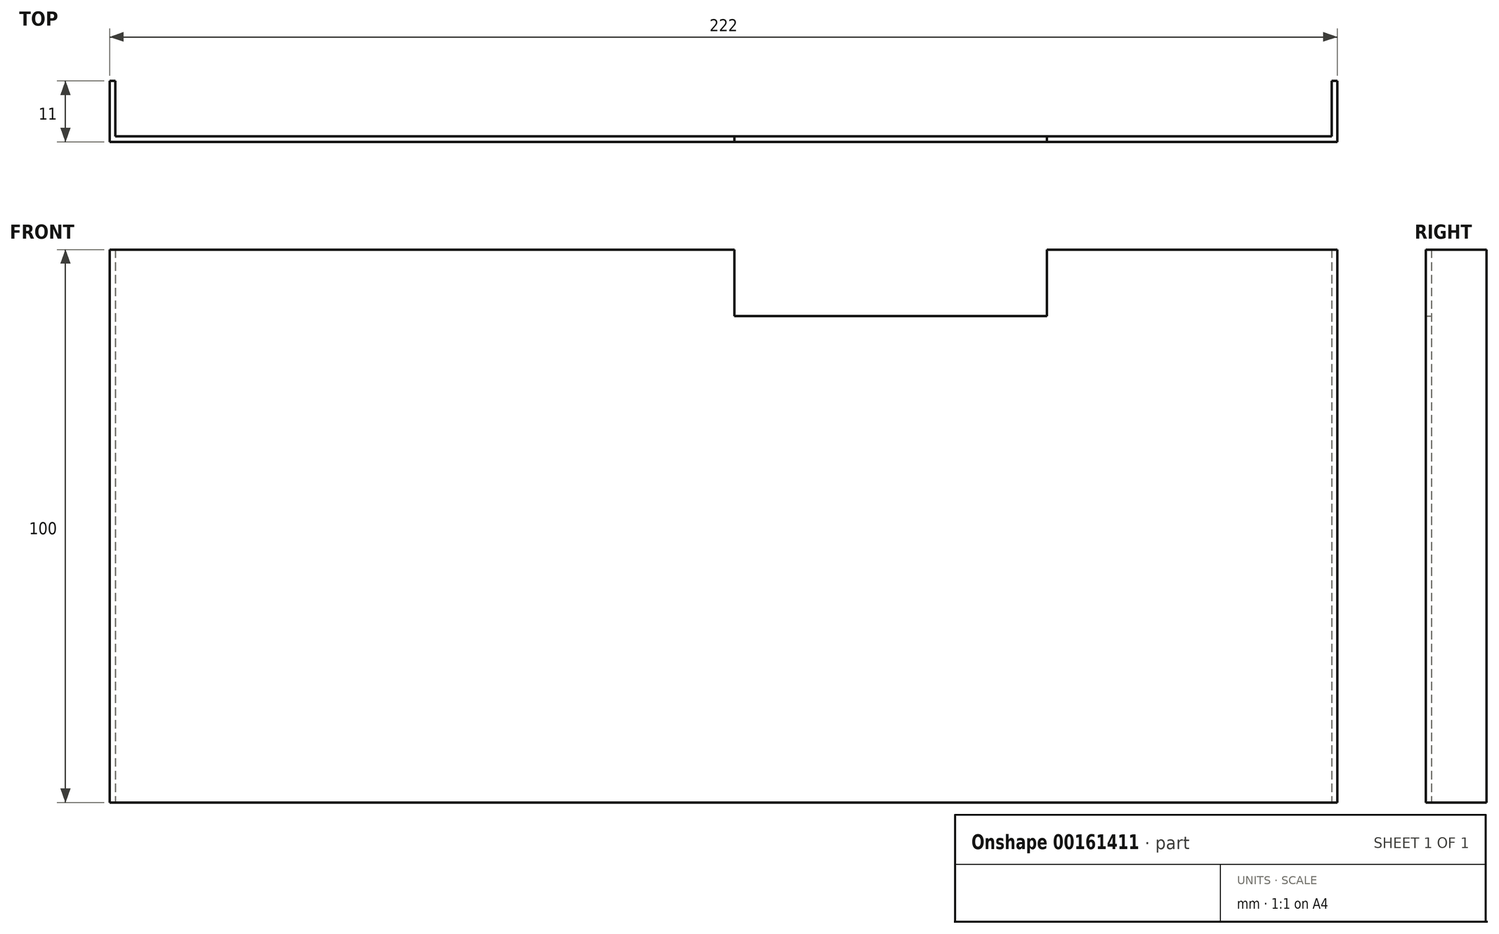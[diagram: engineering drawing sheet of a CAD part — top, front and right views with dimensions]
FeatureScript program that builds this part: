
annotation { "Feature Type Name" : "Feature", "Feature Type Description" : "" }
export const myFeature = defineFeature(function(context is Context, id is Id, definition is map)
    precondition{}
    {
        {
            var Q0;
            Q0=qCreatedBy(makeId("Front.planeOp"),FACE);
            var sketch = newSketch(context, id + "F0", { "sketchPlane" : qUnion([Q0])});
            skLineSegment(sketch, "E0.bottom", {"start": v(111, 45.92) * mm, "end": v(58.5, 45.92) * mm});
            skLineSegment(sketch, "E0.top", {"start": v(111, -54.08) * mm, "end": v(-111, -54.08) * mm});
            skLineSegment(sketch, "E0.left", {"start": v(111, 45.92) * mm, "end": v(111, -54.08) * mm});
            skLineSegment(sketch, "E0.right", {"start": v(-111, 45.92) * mm, "end": v(-111, -54.08) * mm});
            skPoint(sketch, "E0.middle", {"position": v(0, -4.08) * mm});
            skLineSegment(sketch, "E1.top", {"start": v(58.5, 33.92) * mm, "end": v(2, 33.92) * mm});
            skLineSegment(sketch, "E1.left", {"start": v(58.5, 45.92) * mm, "end": v(58.5, 33.92) * mm});
            skLineSegment(sketch, "E1.right", {"start": v(2, 45.92) * mm, "end": v(2, 33.92) * mm});
            skLineSegment(sketch, "E2.trimOffspring", {"start": v(2, 45.92) * mm, "end": v(-111, 45.92) * mm});
            skSolve(sketch);
        }
        {
            var Q0;
            Q0 = qSketchRegion(id + "F0", true);
            extrude(context, id + "F1", {"entities" : qUnion([Q0]), "depth" : 1 * mm});
        }
        {
            var Q0;
            Q0=makeQuery(id+"F1.opExtrude","CAP_FACE",FACE,{"disambiguationData":[OSD([sQuery(id+"F0.wireOp",EDGE,"E0.bottom"),sQuery(id+"F0.wireOp",EDGE,"E0.top"),sQuery(id+"F0.wireOp",EDGE,"E0.left"),sQuery(id+"F0.wireOp",EDGE,"E0.right"),sQuery(id+"F0.wireOp",EDGE,"E1.top"),sQuery(id+"F0.wireOp",EDGE,"E1.left"),sQuery(id+"F0.wireOp",EDGE,"E1.right"),sQuery(id+"F0.wireOp",EDGE,"E2.trimOffspring")])],"isStart":true});
            var sketch = newSketch(context, id + "F2", { "sketchPlane" : qUnion([Q0])});
            skLineSegment(sketch, "E3.bottom", {"start": v(-111, 45.92) * mm, "end": v(-110, 45.92) * mm});
            skLineSegment(sketch, "E3.top", {"start": v(-111, -54.08) * mm, "end": v(-110, -54.08) * mm});
            skLineSegment(sketch, "E3.left", {"start": v(-111, 45.92) * mm, "end": v(-111, -54.08) * mm});
            skLineSegment(sketch, "E3.right", {"start": v(-110, 45.92) * mm, "end": v(-110, -54.08) * mm});
            skLineSegment(sketch, "E4.bottom", {"start": v(111, 45.92) * mm, "end": v(110, 45.92) * mm});
            skLineSegment(sketch, "E4.top", {"start": v(111, -54.08) * mm, "end": v(110, -54.08) * mm});
            skLineSegment(sketch, "E4.left", {"start": v(111, 45.92) * mm, "end": v(111, -54.08) * mm});
            skLineSegment(sketch, "E4.right", {"start": v(110, 45.92) * mm, "end": v(110, -54.08) * mm});
            skSolve(sketch);
        }
        {
            var Q0;
            Q0 = qSketchRegion(id + "F2", true);
            extrude(context, id + "F3", {"entities" : qUnion([Q0]), "operationType" : NewBodyOperationType.ADD, "depth" : 10 * mm});
        }
    });
